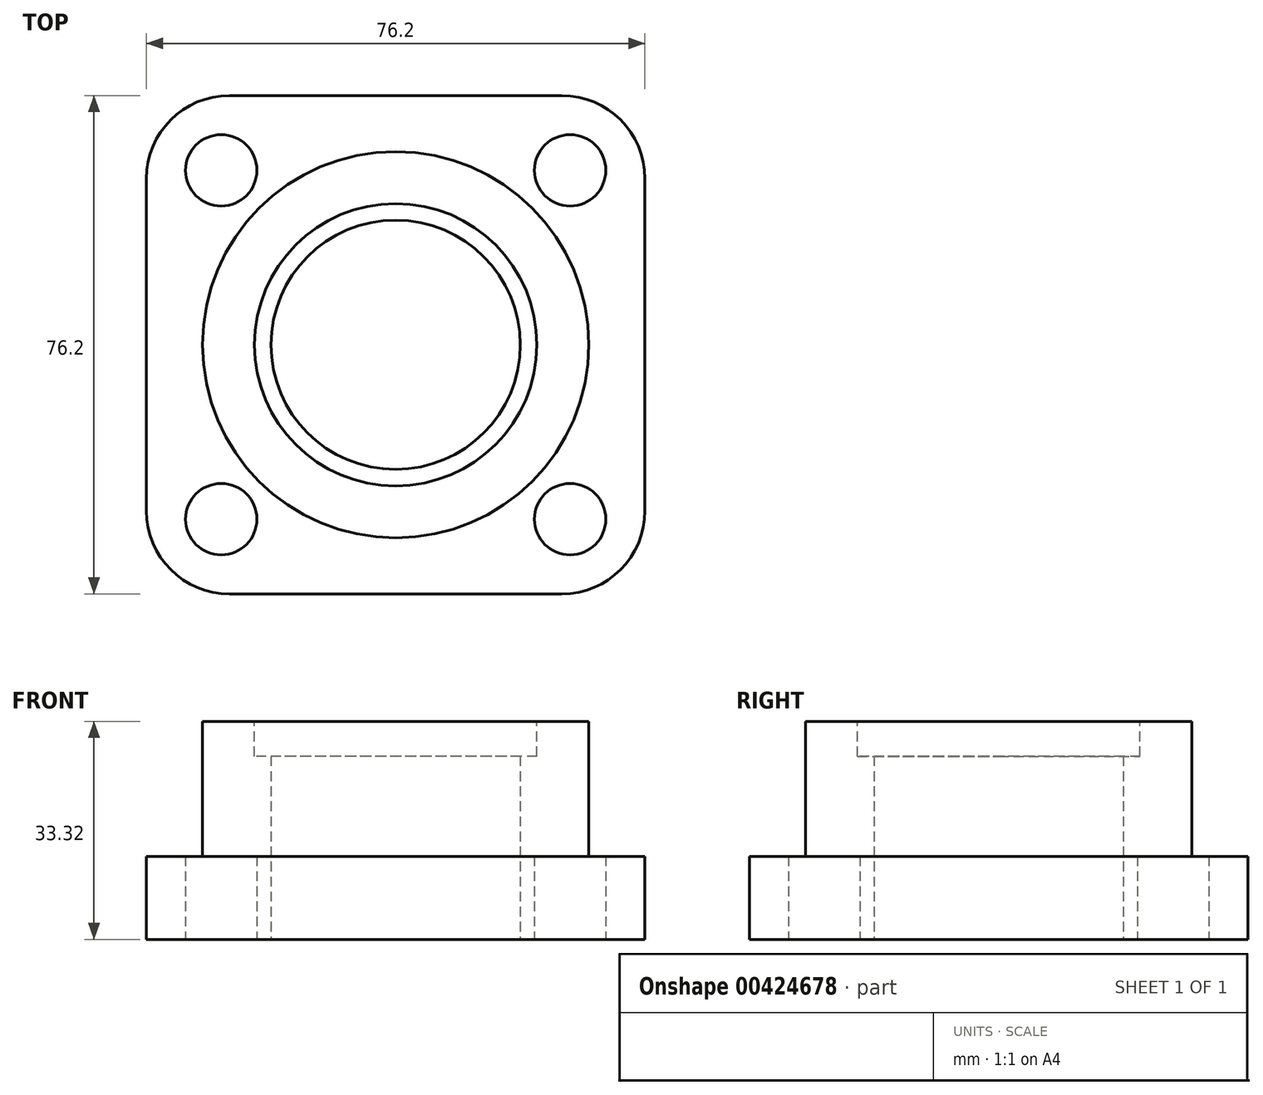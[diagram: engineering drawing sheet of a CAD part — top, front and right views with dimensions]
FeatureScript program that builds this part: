
annotation { "Feature Type Name" : "Feature", "Feature Type Description" : "" }
export const myFeature = defineFeature(function(context is Context, id is Id, definition is map)
    precondition{}
    {
        {
            var Q0;
            Q0=qCreatedBy(makeId("Top.planeOp"),FACE);
            var sketch = newSketch(context, id + "F0", { "sketchPlane" : qUnion([Q0])});
            skLineSegment(sketch, "E0.bottom", {"start": v(12.7, 0) * mm, "end": v(63.5, 0) * mm});
            skLineSegment(sketch, "E0.top", {"start": v(12.7, 76.2) * mm, "end": v(63.5, 76.2) * mm});
            skLineSegment(sketch, "E0.left", {"start": v(0, 12.7) * mm, "end": v(0, 63.5) * mm});
            skLineSegment(sketch, "E0.right", {"start": v(76.2, 12.7) * mm, "end": v(76.2, 63.5) * mm});
            skPoint(sketch, "E1.visualSharp", {"position": v(0, 0) * mm});
            skArc(sketch, "E1.filletArc", {"start": v(0, 12.7) * mm, "mid": v(3.72, 3.72) * mm, "end": v(12.7, 0) * mm});
            skPoint(sketch, "E2.visualSharp", {"position": v(76.2, 0) * mm});
            skArc(sketch, "E2.filletArc", {"start": v(63.5, 0) * mm, "mid": v(72.48, 3.72) * mm, "end": v(76.2, 12.7) * mm});
            skPoint(sketch, "E3.visualSharp", {"position": v(76.2, 76.2) * mm});
            skArc(sketch, "E3.filletArc", {"start": v(76.2, 63.5) * mm, "mid": v(72.48, 72.48) * mm, "end": v(63.5, 76.2) * mm});
            skPoint(sketch, "E4.visualSharp", {"position": v(0, 76.2) * mm});
            skArc(sketch, "E4.filletArc", {"start": v(12.7, 76.2) * mm, "mid": v(3.72, 72.48) * mm, "end": v(0, 63.5) * mm});
            skCircle(sketch, "E5", {"center": v(64.77, 64.77) * mm, "radius": 5.46 * mm});
            skCircle(sketch, "E6", {"center": v(64.77, 11.43) * mm, "radius": 5.46 * mm});
            skCircle(sketch, "E7", {"center": v(11.43, 11.43) * mm, "radius": 5.46 * mm});
            skCircle(sketch, "E8", {"center": v(11.43, 64.77) * mm, "radius": 5.46 * mm});
            skSolve(sketch);
        }
        {
            var Q0;
            Q0 = qSketchRegion(id + "F0", true);
            extrude(context, id + "F1", {"entities" : qUnion([Q0]), "depth" : 12.7 * mm});
        }
        {
            var Q0;
            Q0=makeQuery(id+"F1.opExtrude","CAP_FACE",FACE,{"disambiguationData":[OSD([sQuery(id+"F0.wireOp",EDGE,"E0.bottom"),sQuery(id+"F0.wireOp",EDGE,"E0.top"),sQuery(id+"F0.wireOp",EDGE,"E0.left"),sQuery(id+"F0.wireOp",EDGE,"E0.right"),sQuery(id+"F0.wireOp",EDGE,"E1.filletArc"),sQuery(id+"F0.wireOp",EDGE,"E2.filletArc"),sQuery(id+"F0.wireOp",EDGE,"E3.filletArc"),sQuery(id+"F0.wireOp",EDGE,"E4.filletArc"),sQuery(id+"F0.wireOp",EDGE,"E5"),sQuery(id+"F0.wireOp",EDGE,"E6"),sQuery(id+"F0.wireOp",EDGE,"E7"),sQuery(id+"F0.wireOp",EDGE,"E8")])],"isStart":false});
            var sketch = newSketch(context, id + "F2", { "sketchPlane" : qUnion([Q0])});
            skLineSegment(sketch, "E9", {"start": v(38.1, 76.2) * mm, "end": v(38.1, 0) * mm, "construction": true});
            skCircle(sketch, "E10", {"center": v(38.1, 38.1) * mm, "radius": 29.53 * mm});
            skCircle(sketch, "E11", {"center": v(38.1, 38.1) * mm, "radius": 19.05 * mm});
            skSolve(sketch);
        }
        {
            var Q0;
            Q0 = qSketchRegion(id + "F2", true);
            extrude(context, id + "F3", {"entities" : qUnion([Q0]), "operationType" : NewBodyOperationType.ADD, "depth" : 20.62 * mm});
        }
        {
            var Q0;
            Q0=makeQuery(id+"F3.opExtrude","CAP_FACE",FACE,{"disambiguationData":[OSD([sQuery(id+"F2.wireOp",EDGE,"E10"),sQuery(id+"F2.wireOp",EDGE,"E11")])],"isStart":false});
            var sketch = newSketch(context, id + "F4", { "sketchPlane" : qUnion([Q0])});
            skCircle(sketch, "E12", {"center": v(38.1, 38.1) * mm, "radius": 21.59 * mm});
            skSolve(sketch);
        }
        {
            var Q0;
            Q0 = qSketchRegion(id + "F4", true);
            extrude(context, id + "F5", {"entities" : qUnion([Q0]), "operationType" : NewBodyOperationType.REMOVE, "oppositeDirection" : true, "depth" : 5.33 * mm});
        }
        {
            var Q0;
            Q0=makeQuery(id+"F3.boolean.opBoolean","SPLIT",FACE,{"disambiguationData":[TD([makeQuery(id+"F3.opExtrude","SWEPT_FACE",FACE,{"disambiguationData":[OSD([sQuery(id+"F2.wireOp",EDGE,"E11")])]})])],"derivedFrom":makeQuery(id+"F1.opExtrude","CAP_FACE",FACE,{"disambiguationData":[OSD([sQuery(id+"F0.wireOp",EDGE,"E0.bottom"),sQuery(id+"F0.wireOp",EDGE,"E0.top"),sQuery(id+"F0.wireOp",EDGE,"E0.left"),sQuery(id+"F0.wireOp",EDGE,"E0.right"),sQuery(id+"F0.wireOp",EDGE,"E1.filletArc"),sQuery(id+"F0.wireOp",EDGE,"E2.filletArc"),sQuery(id+"F0.wireOp",EDGE,"E3.filletArc"),sQuery(id+"F0.wireOp",EDGE,"E4.filletArc"),sQuery(id+"F0.wireOp",EDGE,"E5"),sQuery(id+"F0.wireOp",EDGE,"E6"),sQuery(id+"F0.wireOp",EDGE,"E7"),sQuery(id+"F0.wireOp",EDGE,"E8")])],"isStart":false})});
            var sketch = newSketch(context, id + "F6", { "sketchPlane" : qUnion([Q0])});
            skCircle(sketch, "E13.0.0", {"center": v(38.1, 38.1) * mm, "radius": 19.05 * mm});
            skSolve(sketch);
        }
        {
            var Q0;
            Q0 = qSketchRegion(id + "F6", true);
            extrude(context, id + "F7", {"entities" : qUnion([Q0]), "operationType" : NewBodyOperationType.REMOVE, "oppositeDirection" : true, "depth" : 25.4 * mm});
        }
    });
